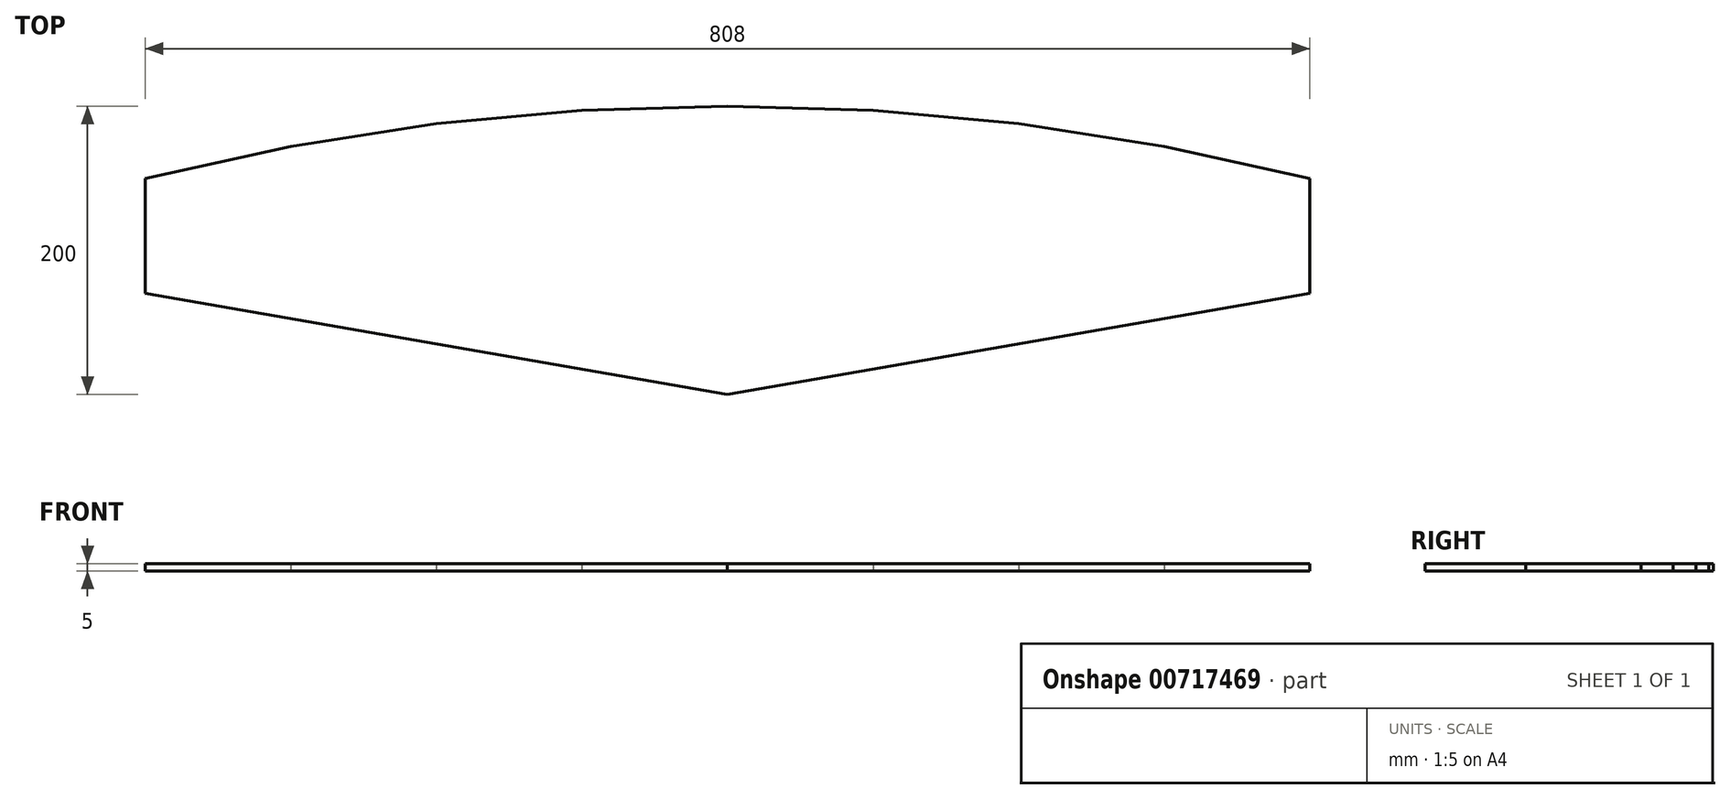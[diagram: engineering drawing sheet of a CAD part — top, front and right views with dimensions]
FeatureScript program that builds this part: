
annotation { "Feature Type Name" : "Feature", "Feature Type Description" : "" }
export const myFeature = defineFeature(function(context is Context, id is Id, definition is map)
    precondition{}
    {
        {
            var Q0;
            Q0=qCreatedBy(makeId("Top.planeOp"),FACE);
            var sketch = newSketch(context, id + "F0", { "sketchPlane" : qUnion([Q0])});
            skLineSegment(sketch, "E0", {"start": v(404, 150) * mm, "end": v(404, 70) * mm});
            skLineSegment(sketch, "E1", {"start": v(0, 0) * mm, "end": v(404, 70) * mm});
            skLineSegment(sketch, "E2", {"start": v(0, 0) * mm, "end": v(0, 200) * mm});
            skLineSegment(sketch, "E3", {"start": v(101, 197) * mm, "end": v(101, 17.5) * mm});
            skLineSegment(sketch, "E4", {"start": v(202, 188) * mm, "end": v(202, 35) * mm});
            skLineSegment(sketch, "E5", {"start": v(303, 172) * mm, "end": v(303, 52.5) * mm});
            skLineSegment(sketch, "E6", {"start": v(0, 200) * mm, "end": v(101, 197) * mm});
            skLineSegment(sketch, "E7", {"start": v(202, 188) * mm, "end": v(101, 197) * mm});
            skLineSegment(sketch, "E8", {"start": v(202, 188) * mm, "end": v(303, 172) * mm});
            skLineSegment(sketch, "E9", {"start": v(303, 172) * mm, "end": v(404, 150) * mm});
            skLineSegment(sketch, "E10.MirrorCS", {"start": v(0, 200) * mm, "end": v(-101, 197) * mm});
            skLineSegment(sketch, "E11.MirrorCS", {"start": v(-202, 188) * mm, "end": v(-101, 197) * mm});
            skLineSegment(sketch, "E12.MirrorCS", {"start": v(-202, 188) * mm, "end": v(-303, 172) * mm});
            skLineSegment(sketch, "E13.MirrorCS", {"start": v(-303, 172) * mm, "end": v(-404, 150) * mm});
            skLineSegment(sketch, "E14.MirrorCS", {"start": v(-404, 150) * mm, "end": v(-404, 70) * mm});
            skLineSegment(sketch, "E15.MirrorCS", {"start": v(0, 0) * mm, "end": v(-404, 70) * mm});
            skLineSegment(sketch, "E16.MirrorCS", {"start": v(-101, 197) * mm, "end": v(-101, 17.5) * mm});
            skLineSegment(sketch, "E17.MirrorCS", {"start": v(-202, 188) * mm, "end": v(-202, 35) * mm});
            skLineSegment(sketch, "E18.MirrorCS", {"start": v(-303, 172) * mm, "end": v(-303, 52.5) * mm});
            skSolve(sketch);
        }
        {
            var Q0;
            Q0 = qSketchRegion(id + "F0", true);
            extrude(context, id + "F1", {"entities" : qUnion([Q0]), "depth" : 5 * mm, "offsetDistance" : 25 * mm});
        }
    });
